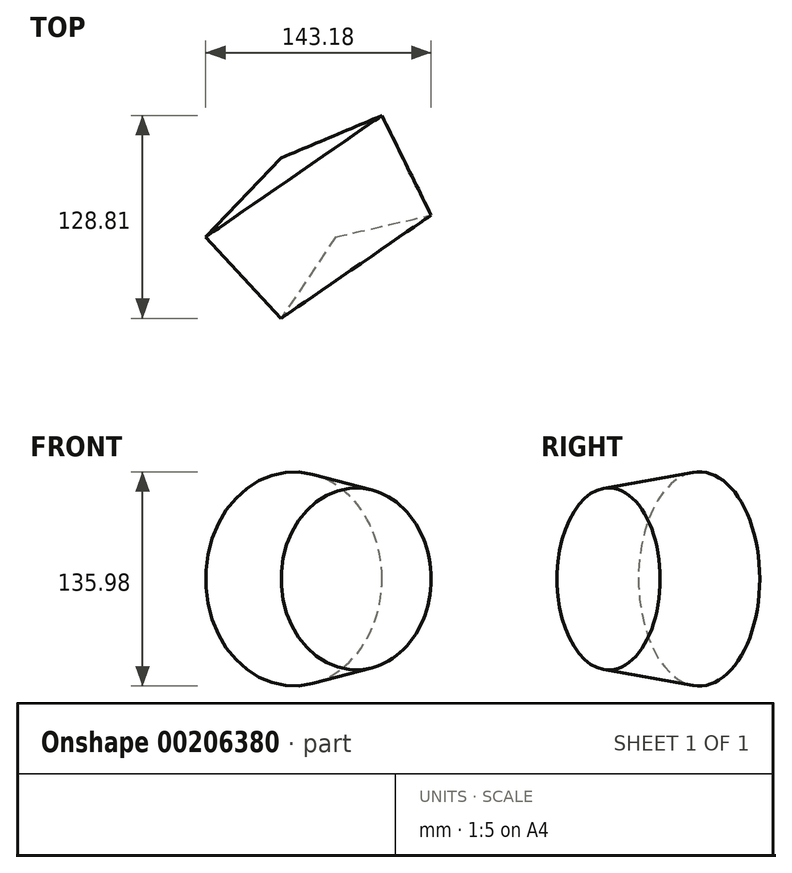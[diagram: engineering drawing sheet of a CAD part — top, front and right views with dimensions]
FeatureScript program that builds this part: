
annotation { "Feature Type Name" : "Feature", "Feature Type Description" : "" }
export const myFeature = defineFeature(function(context is Context, id is Id, definition is map)
    precondition{}
    {
        {
            var Q0;
            Q0=qCreatedBy(makeId("Top.planeOp"),FACE);
            var sketch = newSketch(context, id + "F0", { "sketchPlane" : qUnion([Q0])});
            skLineSegment(sketch, "E0", {"start": v(0, 50.21) * mm, "end": v(-47.98, 0) * mm});
            skLineSegment(sketch, "E1", {"start": v(-47.98, 0) * mm, "end": v(0, -51.7) * mm});
            skLineSegment(sketch, "E2", {"start": v(0, -51.7) * mm, "end": v(34.57, 0) * mm});
            skLineSegment(sketch, "E3", {"start": v(34.57, 0) * mm, "end": v(0, 50.21) * mm});
            skLineSegment(sketch, "E4", {"start": v(34.57, 0) * mm, "end": v(45.6, 18.92) * mm});
            skLineSegment(sketch, "E5", {"start": v(45.6, 18.92) * mm, "end": v(0, 50.21) * mm});
            skLineSegment(sketch, "E6", {"start": v(0, 50.21) * mm, "end": v(-57.8, 17.43) * mm});
            skLineSegment(sketch, "E7", {"start": v(-57.8, 17.43) * mm, "end": v(-47.98, 0) * mm});
            skLineSegment(sketch, "E8", {"start": v(0, -51.7) * mm, "end": v(-17.58, -56.47) * mm});
            skLineSegment(sketch, "E9", {"start": v(-17.58, -56.47) * mm, "end": v(-47.98, 0) * mm});
            skLineSegment(sketch, "E10", {"start": v(0, -51.7) * mm, "end": v(17.58, -56.47) * mm});
            skLineSegment(sketch, "E11", {"start": v(17.58, -56.47) * mm, "end": v(34.57, 0) * mm});
            skSolve(sketch);
        }
        {
            var Q0;
            Q0=makeQuery(id+"F0.imprint","IMPRINT",FACE,{"disambiguationData":[TD([[makeQuery(id+"F0.imprint","IMPRINT",EDGE,{"derivedFrom":sQuery(id+"F0.wireOp",EDGE,"E0")}),1.0]])]});
            var Q1;
            Q1=sQuery(id+"F0.wireOp",EDGE,"E3");
            revolve(context, id + "F1", {"entities" : qUnion([Q0]), "axis" : qUnion([Q1]), "revolveType" : RevolveType.FULL});
        }
    });
